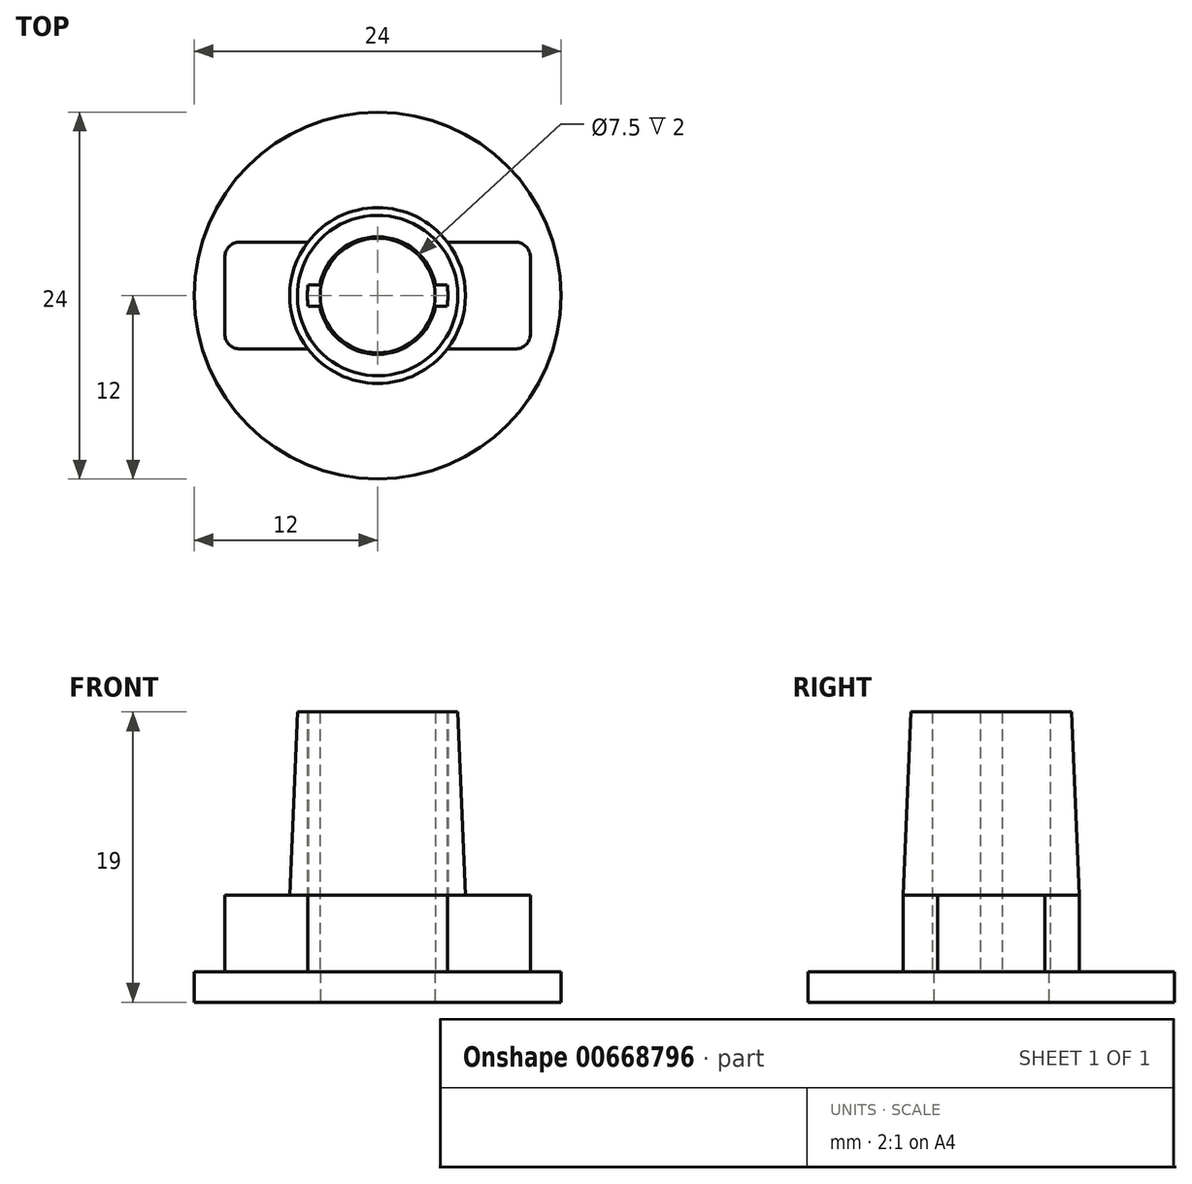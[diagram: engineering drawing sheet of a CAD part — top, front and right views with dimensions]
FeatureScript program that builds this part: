
annotation { "Feature Type Name" : "Feature", "Feature Type Description" : "" }
export const myFeature = defineFeature(function(context is Context, id is Id, definition is map)
    precondition{}
    {
        {
            var Q0;
            Q0=qCreatedBy(makeId("Top.planeOp"),FACE);
            var sketch = newSketch(context, id + "F0", { "sketchPlane" : qUnion([Q0])});
            skCircle(sketch, "E0", {"center": v(0, 0) * mm, "radius": 12 * mm});
            skCircle(sketch, "E1", {"center": v(0, 0) * mm, "radius": 3.75 * mm});
            skSolve(sketch);
        }
        {
            var Q0;
            Q0=qSketchRegion(id+"F0",true);
            extrude(context, id + "F1", {"entities" : qUnion([Q0]), "depth" : 2 * mm, "offsetDistance" : 25 * mm});
        }
        {
            var Q0;
            Q0=makeQuery(id+"F1.opExtrude","CAP_FACE",FACE,{"disambiguationData":[OSD([sQuery(id+"F0.wireOp",EDGE,"E0")])],"isStart":false});
            var sketch = newSketch(context, id + "F2", { "sketchPlane" : qUnion([Q0])});
            skLineSegment(sketch, "E2.top", {"start": v(0, -3.5) * mm, "end": v(9, -3.5) * mm});
            skLineSegment(sketch, "E2.right", {"start": v(10, 0) * mm, "end": v(10, -2.5) * mm});
            skLineSegment(sketch, "E3.MirrorCS", {"start": v(0, 3.5) * mm, "end": v(9, 3.5) * mm});
            skLineSegment(sketch, "E4.MirrorCS", {"start": v(10, 0) * mm, "end": v(10, 2.5) * mm});
            skLineSegment(sketch, "E5.MirrorCS", {"start": v(0, -3.5) * mm, "end": v(-9, -3.5) * mm});
            skLineSegment(sketch, "E6.MirrorCS", {"start": v(-10, 0) * mm, "end": v(-10, -2.5) * mm});
            skLineSegment(sketch, "E7.MirrorCS", {"start": v(-10, 0) * mm, "end": v(-10, 2.5) * mm});
            skLineSegment(sketch, "E8.MirrorCS", {"start": v(0, 3.5) * mm, "end": v(-9, 3.5) * mm});
            skPoint(sketch, "E9.visualSharp", {"position": v(-10, 3.5) * mm});
            skArc(sketch, "E9.filletArc", {"start": v(-9, 3.5) * mm, "mid": v(-9.7, 3.2) * mm, "end": v(-10, 2.5) * mm});
            skPoint(sketch, "E10.visualSharp", {"position": v(-10, -3.5) * mm});
            skArc(sketch, "E10.filletArc", {"start": v(-10, -2.5) * mm, "mid": v(-9.7, -3.2) * mm, "end": v(-9, -3.5) * mm});
            skPoint(sketch, "E11.visualSharp", {"position": v(10, -3.5) * mm});
            skArc(sketch, "E11.filletArc", {"start": v(9, -3.5) * mm, "mid": v(9.7, -3.2) * mm, "end": v(10, -2.5) * mm});
            skPoint(sketch, "E12.visualSharp", {"position": v(10, 3.5) * mm});
            skArc(sketch, "E12.filletArc", {"start": v(10, 2.5) * mm, "mid": v(9.7, 3.2) * mm, "end": v(9, 3.5) * mm});
            skCircle(sketch, "E13", {"center": v(0, 0) * mm, "radius": 5.75 * mm});
            skLineSegment(sketch, "E14.0", {"start": v(4.55, -0.7) * mm, "end": v(3.79, -0.7) * mm});
            skLineSegment(sketch, "E15.MirrorCS", {"start": v(4.55, 0.7) * mm, "end": v(3.79, 0.7) * mm});
            skLineSegment(sketch, "E16.MirrorCS", {"start": v(4, -0.7) * mm, "end": v(3.79, -0.7) * mm});
            skLineSegment(sketch, "E17.trimOffspring", {"start": v(-3.79, 0.7) * mm, "end": v(-4.55, 0.7) * mm});
            skLineSegment(sketch, "E18.trimOffspring", {"start": v(-3.79, -0.7) * mm, "end": v(-4, -0.7) * mm});
            skLineSegment(sketch, "E19.trimOffspring", {"start": v(-3.79, -0.7) * mm, "end": v(-4.55, -0.7) * mm});
            skArc(sketch, "E20.0", {"start": v(3.79, 0.7) * mm, "mid": v(0, 3.85) * mm, "end": v(-3.79, 0.7) * mm});
            skArc(sketch, "E21.0", {"start": v(-3.79, -0.7) * mm, "mid": v(0, -3.85) * mm, "end": v(3.79, -0.7) * mm});
            skArc(sketch, "E22.0", {"start": v(-4.55, 0.7) * mm, "mid": v(-4.6, 0) * mm, "end": v(-4.55, -0.7) * mm});
            skArc(sketch, "E23.0", {"start": v(4.55, -0.7) * mm, "mid": v(4.6, 0) * mm, "end": v(4.55, 0.7) * mm});
            skSolve(sketch);
        }
        {
            var Q0;
            Q0=makeQuery(id+"F2.imprint","IMPRINT",FACE,{"disambiguationData":[TD([[makeQuery(id+"F2.imprint","IMPRINT",EDGE,{"derivedFrom":sQuery(id+"F2.wireOp",EDGE,"E6.MirrorCS")}),1.0]])]});
            var Q1;
            {var subQ0=sQuery(id+"F2.wireOp",EDGE,"E17.trimOffspring");Q1=makeQuery(id+"F2.imprint","IMPRINT",FACE,{"disambiguationData":[TD([[makeQuery(id+"F2.imprint","IMPRINT",EDGE,{"derivedFrom":subQ0}),-1.0]])]});}
            var Q2;
            {var subQ0=sQuery(id+"F2.wireOp",EDGE,"E21.0");var subQ1=sQuery(id+"F2.wireOp",EDGE,"E2.top");var subQ2=makeQuery(id+"F2.imprint","INTERSECT",VERTEX,{"derivedFrom":[subQ1,subQ0]});Q2=makeQuery(id+"F2.imprint","IMPRINT",FACE,{"disambiguationData":[TD([[makeQuery(id+"F2.imprint","IMPRINT",EDGE,{"disambiguationData":[TD([[subQ2,-1.0]])],"derivedFrom":subQ1}),-1.0]])]});}
            var Q3;
            Q3=makeQuery(id+"F2.imprint","IMPRINT",FACE,{"disambiguationData":[TD([[makeQuery(id+"F2.imprint","IMPRINT",EDGE,{"derivedFrom":sQuery(id+"F2.wireOp",EDGE,"E2.right")}),-1.0]])]});
            var Q4;
            Q4=makeQuery(id+"F2.imprint","IMPRINT",FACE,{"disambiguationData":[TD([[makeQuery(id+"F2.imprint","IMPRINT",EDGE,{"derivedFrom":sQuery(id+"F2.wireOp",EDGE,"E14.0")}),1.0]])]});
            var Q5;
            {var subQ0=sQuery(id+"F2.wireOp",EDGE,"E20.0");var subQ1=sQuery(id+"F2.wireOp",EDGE,"E3.MirrorCS");var subQ2=makeQuery(id+"F2.imprint","INTERSECT",VERTEX,{"derivedFrom":[subQ1,subQ0]});Q5=makeQuery(id+"F2.imprint","IMPRINT",FACE,{"disambiguationData":[TD([[makeQuery(id+"F2.imprint","IMPRINT",EDGE,{"disambiguationData":[TD([[subQ2,-1.0]])],"derivedFrom":subQ1}),1.0]])]});}
            extrude(context, id + "F3", {"entities" : qUnion([Q0, Q1, Q2, Q3, Q4, Q5]), "operationType" : NewBodyOperationType.ADD, "depth" : 5 * mm, "offsetDistance" : 25 * mm});
        }
        {
            var Q0;
            Q0=makeQuery(id+"F3.opExtrude","CAP_FACE",FACE,{"disambiguationData":[OSD([sQuery(id+"F2.wireOp",EDGE,"E2.top"),sQuery(id+"F2.wireOp",EDGE,"E2.right"),sQuery(id+"F2.wireOp",EDGE,"E3.MirrorCS"),sQuery(id+"F2.wireOp",EDGE,"E4.MirrorCS"),sQuery(id+"F2.wireOp",EDGE,"E5.MirrorCS"),sQuery(id+"F2.wireOp",EDGE,"E6.MirrorCS"),sQuery(id+"F2.wireOp",EDGE,"E7.MirrorCS"),sQuery(id+"F2.wireOp",EDGE,"E8.MirrorCS"),sQuery(id+"F2.wireOp",EDGE,"E9.filletArc"),sQuery(id+"F2.wireOp",EDGE,"E10.filletArc"),sQuery(id+"F2.wireOp",EDGE,"E11.filletArc"),sQuery(id+"F2.wireOp",EDGE,"E12.filletArc"),sQuery(id+"F2.wireOp",EDGE,"E13"),sQuery(id+"F2.wireOp",EDGE,"E14.0"),sQuery(id+"F2.wireOp",EDGE,"E15.MirrorCS"),sQuery(id+"F2.wireOp",EDGE,"E16.MirrorCS"),sQuery(id+"F2.wireOp",EDGE,"E17.trimOffspring"),sQuery(id+"F2.wireOp",EDGE,"E19.trimOffspring"),sQuery(id+"F2.wireOp",EDGE,"E20.0"),sQuery(id+"F2.wireOp",EDGE,"E21.0"),sQuery(id+"F2.wireOp",EDGE,"E22.0"),sQuery(id+"F2.wireOp",EDGE,"E23.0")])],"isStart":false});
            var sketch = newSketch(context, id + "F4", { "sketchPlane" : qUnion([Q0])});
            skCircle(sketch, "E24", {"center": v(0, 0) * mm, "radius": 5.75 * mm});
            skSolve(sketch);
        }
        {
            var Q0;
            Q0=makeQuery(id+"F4.imprint","IMPRINT",FACE,{"disambiguationData":[TD([[makeQuery(id+"F4.imprint","IMPRINT",EDGE,{"derivedFrom":makeQuery(id+"F3.opExtrude","CAP_EDGE",EDGE,{"disambiguationData":[OSD([sQuery(id+"F2.wireOp",EDGE,"E15.MirrorCS")])],"isStart":false})}),-1.0]])]});
            extrude(context, id + "F5", {"entities" : qUnion([Q0]), "operationType" : NewBodyOperationType.ADD, "depth" : 12 * mm, "offsetDistance" : 25 * mm});
        }
        {
            var Q0;
            Q0=makeQuery(id+"F5.opExtrude","CAP_EDGE",EDGE,{"disambiguationData":[OSD([sQuery(id+"F4.wireOp",EDGE,"E24")])],"isStart":false});
            chamfer(context, id + "F6", {"entities" : qUnion([Q0]), "chamferType" : ChamferType.TWO_OFFSETS, "width1" : 0.5 * mm, "oppositeDirection" : false, "width2" : 12 * mm, "tangentPropagation" : true});
        }
    });
